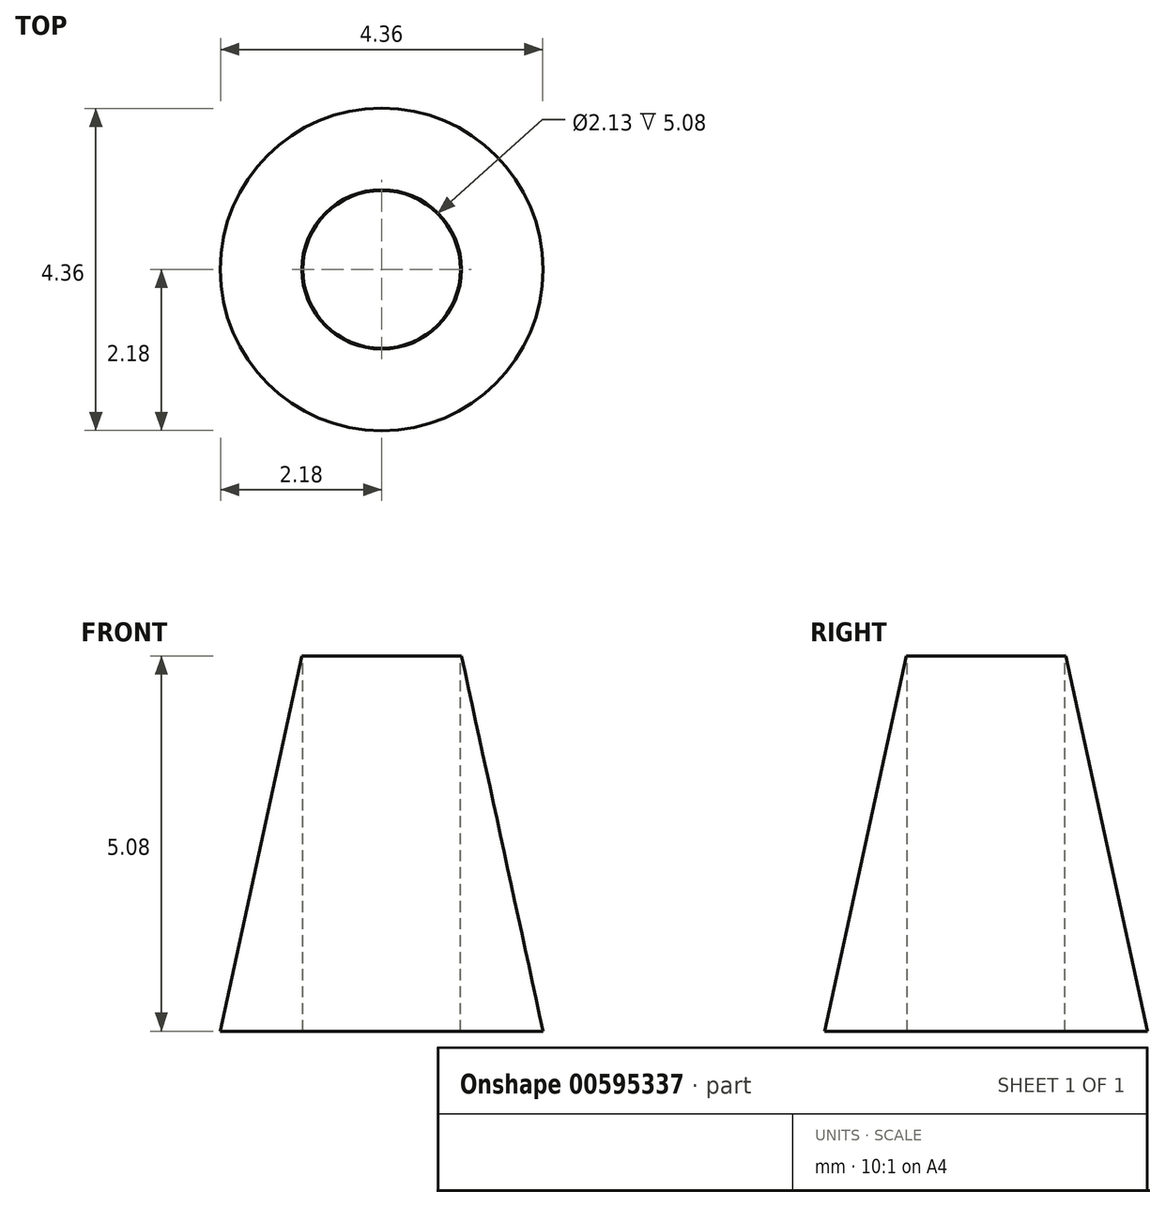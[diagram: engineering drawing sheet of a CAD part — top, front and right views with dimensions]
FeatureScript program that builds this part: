
annotation { "Feature Type Name" : "Feature", "Feature Type Description" : "" }
export const myFeature = defineFeature(function(context is Context, id is Id, definition is map)
    precondition{}
    {
        {
            var Q0;
            Q0=qCreatedBy(makeId("Top.planeOp"),FACE);
            var sketch = newSketch(context, id + "F0", { "sketchPlane" : qUnion([Q0])});
            skCircle(sketch, "E0", {"center": v(0, 0) * mm, "radius": 2.18 * mm});
            skSolve(sketch);
        }
        {
            var Q0;
            Q0=qCreatedBy(makeId("Top.planeOp"),FACE);
            cPlane(context, id + "F1", {"entities" : qUnion([Q0]), "cplaneType" : CPlaneType.OFFSET, "offset" : 5.08 * mm, "width" : 152.4 * mm, "height" : 152.4 * mm});
        }
        {
            var Q0;
            Q0=qCreatedBy(id+"F1.planeOp",FACE);
            var sketch = newSketch(context, id + "F2", { "sketchPlane" : qUnion([Q0])});
            skCircle(sketch, "E1", {"center": v(0, 0) * mm, "radius": 1.08 * mm});
            skSolve(sketch);
        }
        {
            var Q0;
            Q0=makeQuery(id+"F0.imprint","IMPRINT",FACE,{"disambiguationData":[TD([[makeQuery(id+"F0.imprint","IMPRINT",EDGE,{"derivedFrom":sQuery(id+"F0.wireOp",EDGE,"E0")}),1.0]])]});
            var Q1;
            Q1=makeQuery(id+"F2.imprint","IMPRINT",FACE,{"disambiguationData":[TD([[makeQuery(id+"F2.imprint","IMPRINT",EDGE,{"derivedFrom":sQuery(id+"F2.wireOp",EDGE,"E1")}),1.0]])]});
            loft(context, id + "F3", {"sheetProfilesArray" : [{ "sheetProfileEntities" : qUnion([Q0]) }, { "sheetProfileEntities" : qUnion([Q1]) }]});
        }
        {
            var Q0;
            Q0=makeQuery(id+"F3.opLoft","CAP_FACE",FACE,{"disambiguationData":[OSD([makeQuery(id+"F2.imprint","IMPRINT",FACE,{"disambiguationData":[TD([[makeQuery(id+"F2.imprint","IMPRINT",EDGE,{"derivedFrom":sQuery(id+"F2.wireOp",EDGE,"E1")}),1.0]])]})])],"isStart":true});
            var sketch = newSketch(context, id + "F4", { "sketchPlane" : qUnion([Q0])});
            skCircle(sketch, "E2", {"center": v(0, 0) * mm, "radius": 1.07 * mm});
            skSolve(sketch);
        }
        {
            var Q0;
            Q0=makeQuery(id+"F4.imprint","IMPRINT",FACE,{"disambiguationData":[TD([[makeQuery(id+"F4.imprint","IMPRINT",EDGE,{"derivedFrom":sQuery(id+"F4.wireOp",EDGE,"E2")}),1.0]])]});
            extrude(context, id + "F5", {"entities" : qUnion([Q0]), "operationType" : NewBodyOperationType.REMOVE, "oppositeDirection" : true, "depth" : 127 * mm, "offsetDistance" : 25.4 * mm});
        }
    });
